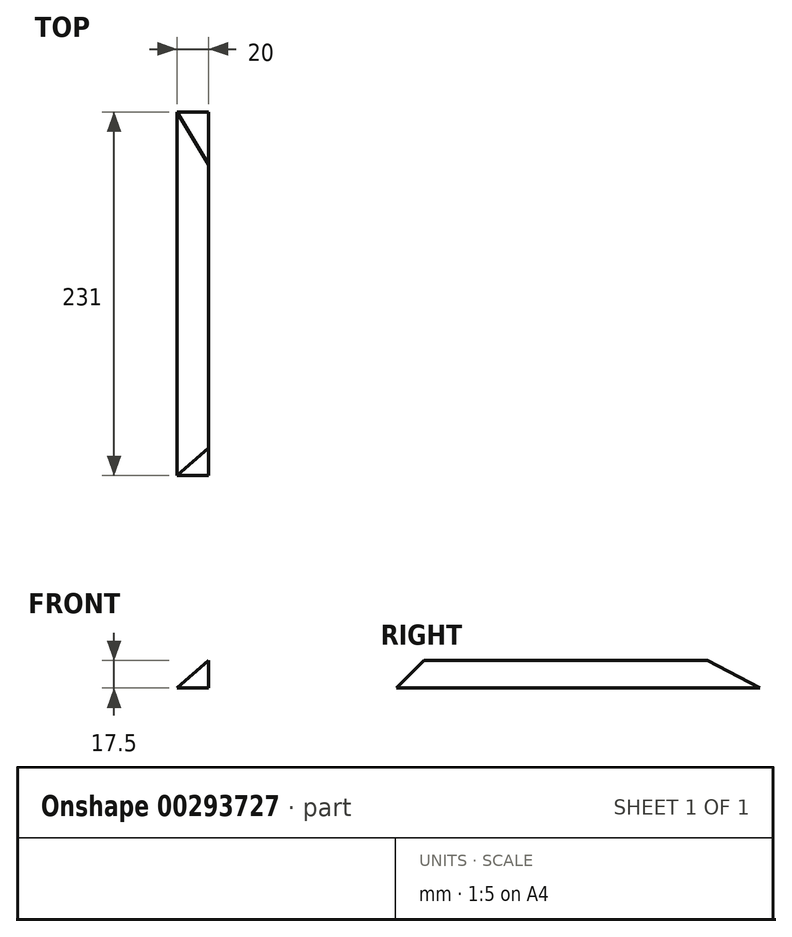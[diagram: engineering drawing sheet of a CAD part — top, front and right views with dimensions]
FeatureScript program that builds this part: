
annotation { "Feature Type Name" : "Feature", "Feature Type Description" : "" }
export const myFeature = defineFeature(function(context is Context, id is Id, definition is map)
    precondition{}
    {
        {
            var Q0;
            Q0=qCreatedBy(makeId("Top.planeOp"),FACE);
            var sketch = newSketch(context, id + "F0", { "sketchPlane" : qUnion([Q0])});
            skLineSegment(sketch, "E0.bottom", {"start": v(-10, 115.5) * mm, "end": v(10, 115.5) * mm});
            skLineSegment(sketch, "E0.top", {"start": v(-10, -115.5) * mm, "end": v(10, -115.5) * mm});
            skLineSegment(sketch, "E0.left", {"start": v(-10, 115.5) * mm, "end": v(-10, -115.5) * mm});
            skLineSegment(sketch, "E0.right", {"start": v(10, 115.5) * mm, "end": v(10, -115.5) * mm});
            skPoint(sketch, "E0.middle", {"position": v(0, 0) * mm});
            skSolve(sketch);
        }
        {
            var Q0;
            Q0=qSketchRegion(id+"F0",true);
            extrude(context, id + "F1", {"entities" : qUnion([Q0]), "endBound" : BoundingType.SYMMETRIC, "depth" : 17.5 * mm});
        }
        {
            var Q0;
            Q0=makeQuery(id+"F1.opExtrude","CAP_EDGE",EDGE,{"disambiguationData":[OSD([sQuery(id+"F0.wireOp",EDGE,"E0.top")])],"isStart":false});
            chamfer(context, id + "F2", {"entities" : qUnion([Q0]), "chamferType" : ChamferType.TWO_OFFSETS, "width1" : 17.5 * mm, "oppositeDirection" : false, "width2" : 17.5 * mm, "tangentPropagation" : true});
        }
        {
            var Q0;
            Q0=makeQuery(id+"F1.opExtrude","CAP_EDGE",EDGE,{"disambiguationData":[OSD([sQuery(id+"F0.wireOp",EDGE,"E0.bottom")])],"isStart":false});
            chamfer(context, id + "F3", {"entities" : qUnion([Q0]), "chamferType" : ChamferType.TWO_OFFSETS, "width1" : 17.5 * mm, "oppositeDirection" : false, "width2" : 33.5 * mm, "tangentPropagation" : true});
        }
        {
            var Q0;
            Q0=makeQuery(id+"F1.opExtrude","CAP_EDGE",EDGE,{"disambiguationData":[OSD([sQuery(id+"F0.wireOp",EDGE,"E0.left")])],"isStart":false});
            chamfer(context, id + "F4", {"entities" : qUnion([Q0]), "chamferType" : ChamferType.TWO_OFFSETS, "width1" : 20 * mm, "oppositeDirection" : false, "width2" : 17.5 * mm, "tangentPropagation" : true});
        }
    });
